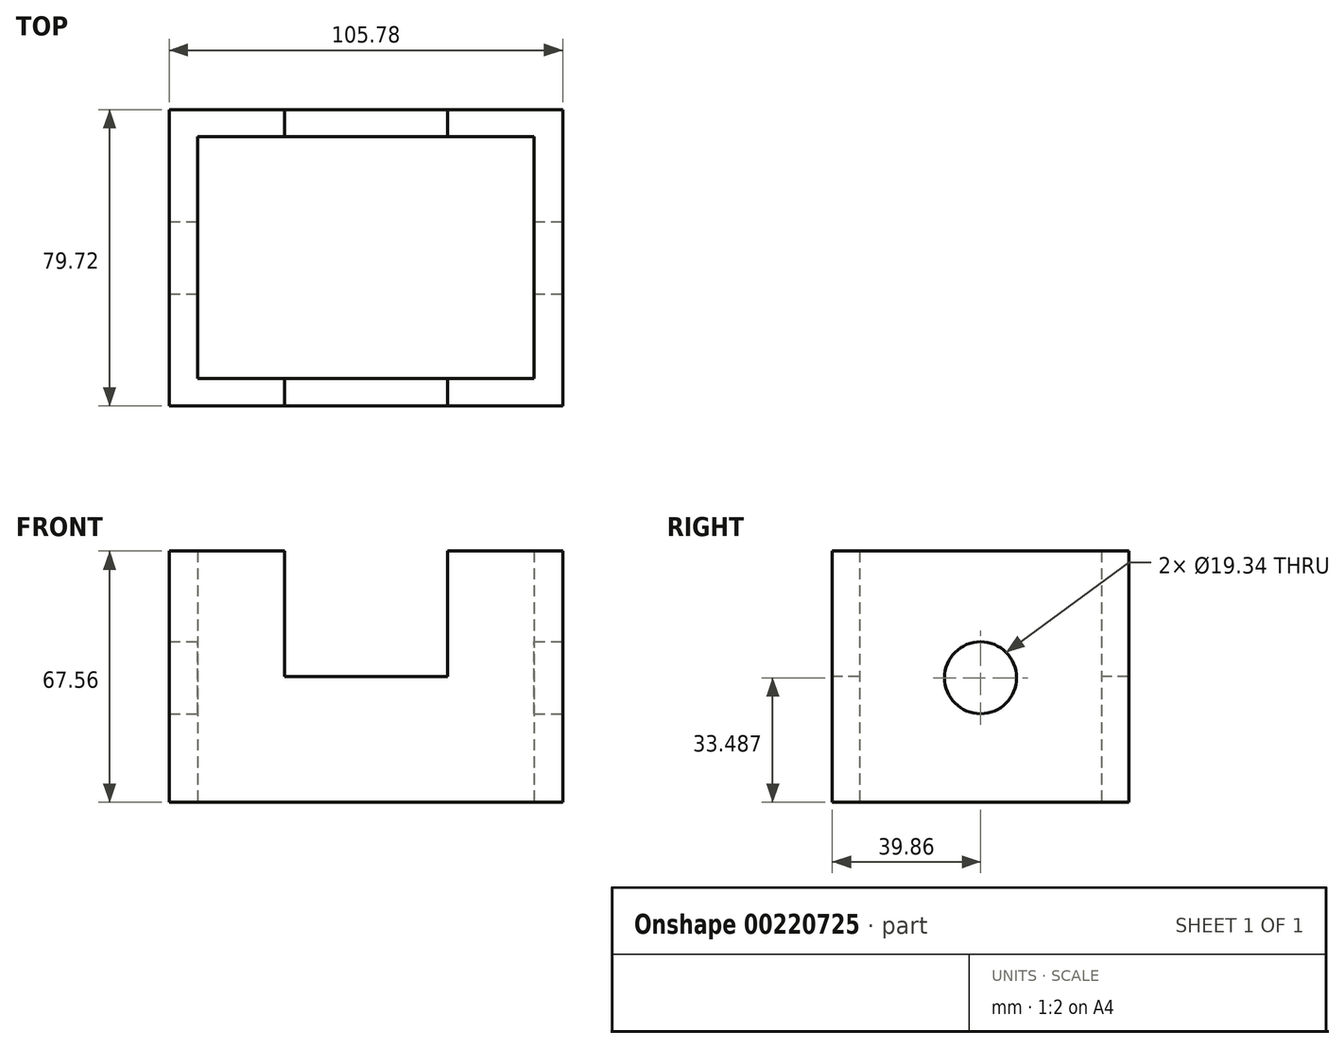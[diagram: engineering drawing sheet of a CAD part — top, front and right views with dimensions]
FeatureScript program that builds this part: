
annotation { "Feature Type Name" : "Feature", "Feature Type Description" : "" }
export const myFeature = defineFeature(function(context is Context, id is Id, definition is map)
    precondition{}
    {
        {
            var Q0;
            Q0=qCreatedBy(makeId("Top.planeOp"),FACE);
            var sketch = newSketch(context, id + "F0", { "sketchPlane" : qUnion([Q0])});
            skLineSegment(sketch, "E0.bottom", {"start": v(52.89, 39.86) * mm, "end": v(-52.89, 39.86) * mm});
            skLineSegment(sketch, "E0.top", {"start": v(52.89, -39.86) * mm, "end": v(-52.89, -39.86) * mm});
            skLineSegment(sketch, "E0.left", {"start": v(52.89, 39.86) * mm, "end": v(52.89, -39.86) * mm});
            skLineSegment(sketch, "E0.right", {"start": v(-52.89, 39.86) * mm, "end": v(-52.89, -39.86) * mm});
            skPoint(sketch, "E0.middle", {"position": v(0, 0) * mm});
            skLineSegment(sketch, "E1.bottom", {"start": v(45.17, 32.53) * mm, "end": v(-45.17, 32.53) * mm});
            skLineSegment(sketch, "E1.top", {"start": v(45.17, -32.53) * mm, "end": v(-45.17, -32.53) * mm});
            skLineSegment(sketch, "E1.left", {"start": v(45.17, 32.53) * mm, "end": v(45.17, -32.53) * mm});
            skLineSegment(sketch, "E1.right", {"start": v(-45.17, 32.53) * mm, "end": v(-45.17, -32.53) * mm});
            skSolve(sketch);
        }
        {
            var Q0;
            Q0=makeQuery(id+"F0.imprint","IMPRINT",FACE,{"disambiguationData":[TD([[makeQuery(id+"F0.imprint","IMPRINT",EDGE,{"derivedFrom":sQuery(id+"F0.wireOp",EDGE,"E0.bottom")}),1.0]])]});
            extrude(context, id + "F1", {"entities" : qUnion([Q0]), "depth" : 67.56 * mm});
        }
        {
            var Q0;
            Q0=makeQuery(id+"F1.opExtrude","SWEPT_FACE",FACE,{"disambiguationData":[OSD([sQuery(id+"F0.wireOp",EDGE,"E0.top")])]});
            var sketch = newSketch(context, id + "F2", { "sketchPlane" : qUnion([Q0])});
            skLineSegment(sketch, "E2.bottom", {"start": v(21.92, 101.32) * mm, "end": v(-21.92, 101.32) * mm});
            skLineSegment(sketch, "E2.top", {"start": v(21.92, 33.8) * mm, "end": v(-21.92, 33.8) * mm});
            skLineSegment(sketch, "E2.left", {"start": v(21.92, 101.32) * mm, "end": v(21.92, 33.8) * mm});
            skLineSegment(sketch, "E2.right", {"start": v(-21.92, 101.32) * mm, "end": v(-21.92, 33.8) * mm});
            skPoint(sketch, "E2.middle", {"position": v(0, 67.56) * mm});
            skSolve(sketch);
        }
        {
            var Q0;
            {var subQ0=sQuery(id+"F2.wireOp",EDGE,"E2.top");Q0=makeQuery(id+"F2.imprint","IMPRINT",FACE,{"disambiguationData":[TD([[makeQuery(id+"F2.imprint","IMPRINT",EDGE,{"derivedFrom":subQ0}),-1.0]])]});}
            extrude(context, id + "F3", {"entities" : qUnion([Q0]), "operationType" : NewBodyOperationType.REMOVE, "oppositeDirection" : true, "depth" : 96.01 * mm});
        }
        {
            var Q0;
            Q0=makeQuery(id+"F1.opExtrude","SWEPT_FACE",FACE,{"disambiguationData":[OSD([sQuery(id+"F0.wireOp",EDGE,"E0.left")])]});
            var sketch = newSketch(context, id + "F4", { "sketchPlane" : qUnion([Q0])});
            skCircle(sketch, "E3", {"center": v(0, 33.49) * mm, "radius": 9.67 * mm});
            skSolve(sketch);
        }
        {
            var Q0;
            Q0=makeQuery(id+"F4.imprint","IMPRINT",FACE,{"disambiguationData":[TD([[makeQuery(id+"F4.imprint","IMPRINT",EDGE,{"derivedFrom":sQuery(id+"F4.wireOp",EDGE,"E3")}),1.0]])]});
            extrude(context, id + "F5", {"entities" : qUnion([Q0]), "operationType" : NewBodyOperationType.REMOVE, "oppositeDirection" : true, "depth" : 129.03 * mm});
        }
    });
